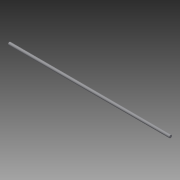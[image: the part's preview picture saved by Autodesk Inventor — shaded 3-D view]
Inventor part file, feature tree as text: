
AUTODESK INVENTOR PART (.ipt)
format: ipt  version: 2013 (Build 170138000, 138)  size: 61,952 bytes
history: native  units: in
note: dims shown in document units (in); Inventor stores cm internally (conversion verified against a paired STEP export)
features: extrude x1, sketch x1
ambient origin geometry x8: Origin, YZ Plane, XZ Plane, XY Plane, X Axis, Y Axis, Z Axis, Center Point
bodies: Solid1 (feature_tree)
feature tree (2):
  extrude  "Extrusion1"  Depth=14.5in TaperAngle=0.0deg
  sketch  "Sketch1"  dims[d0=0.25in d1=14.5in d2=0.0in]
